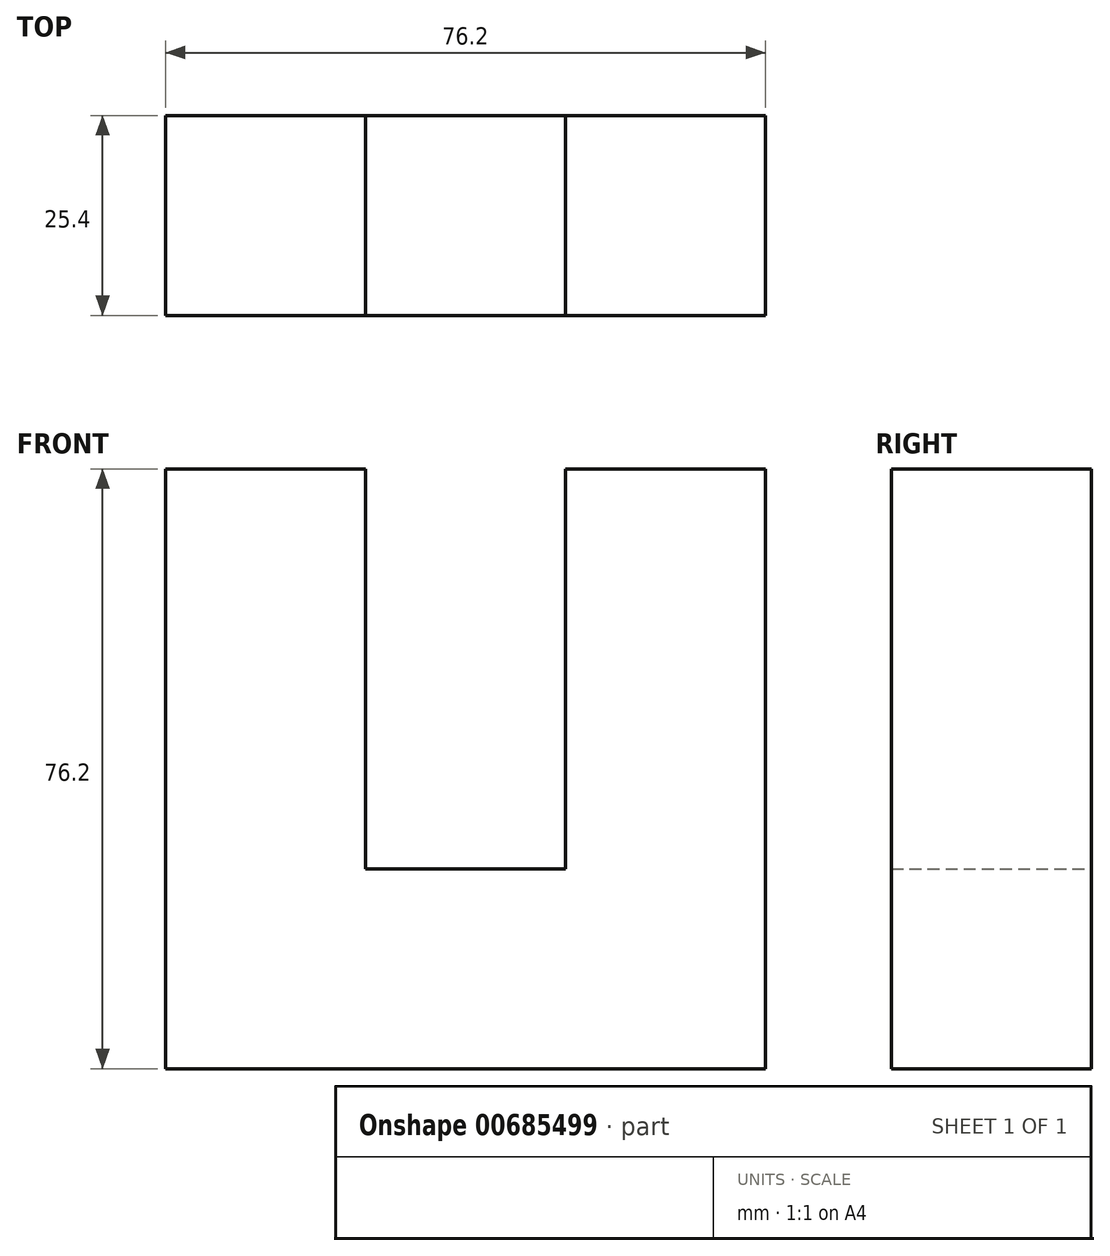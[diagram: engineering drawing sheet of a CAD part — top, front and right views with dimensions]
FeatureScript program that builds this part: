
annotation { "Feature Type Name" : "Feature", "Feature Type Description" : "" }
export const myFeature = defineFeature(function(context is Context, id is Id, definition is map)
    precondition{}
    {
        {
            var Q0;
            Q0=qCreatedBy(makeId("Front.planeOp"),FACE);
            var sketch = newSketch(context, id + "F0", { "sketchPlane" : qUnion([Q0])});
            skLineSegment(sketch, "E0", {"start": v(-40.39, 61.21) * mm, "end": v(-40.39, -14.99) * mm});
            skLineSegment(sketch, "E1", {"start": v(-40.39, -14.99) * mm, "end": v(35.81, -14.99) * mm});
            skLineSegment(sketch, "E2", {"start": v(35.81, -14.99) * mm, "end": v(35.81, 61.21) * mm});
            skLineSegment(sketch, "E3", {"start": v(35.81, 61.21) * mm, "end": v(10.41, 61.21) * mm});
            skLineSegment(sketch, "E4", {"start": v(10.41, 61.21) * mm, "end": v(10.41, 10.41) * mm});
            skLineSegment(sketch, "E5", {"start": v(10.41, 10.41) * mm, "end": v(-14.99, 10.41) * mm});
            skLineSegment(sketch, "E6", {"start": v(-14.99, 10.41) * mm, "end": v(-14.99, 61.21) * mm});
            skLineSegment(sketch, "E7", {"start": v(-14.99, 61.21) * mm, "end": v(-40.39, 61.21) * mm});
            skSolve(sketch);
        }
        {
            var Q0;
            Q0 = qSketchRegion(id + "F0", true);
            extrude(context, id + "F1", {"entities" : qUnion([Q0]), "depth" : 25.4 * mm, "offsetDistance" : 25.4 * mm});
        }
    });
